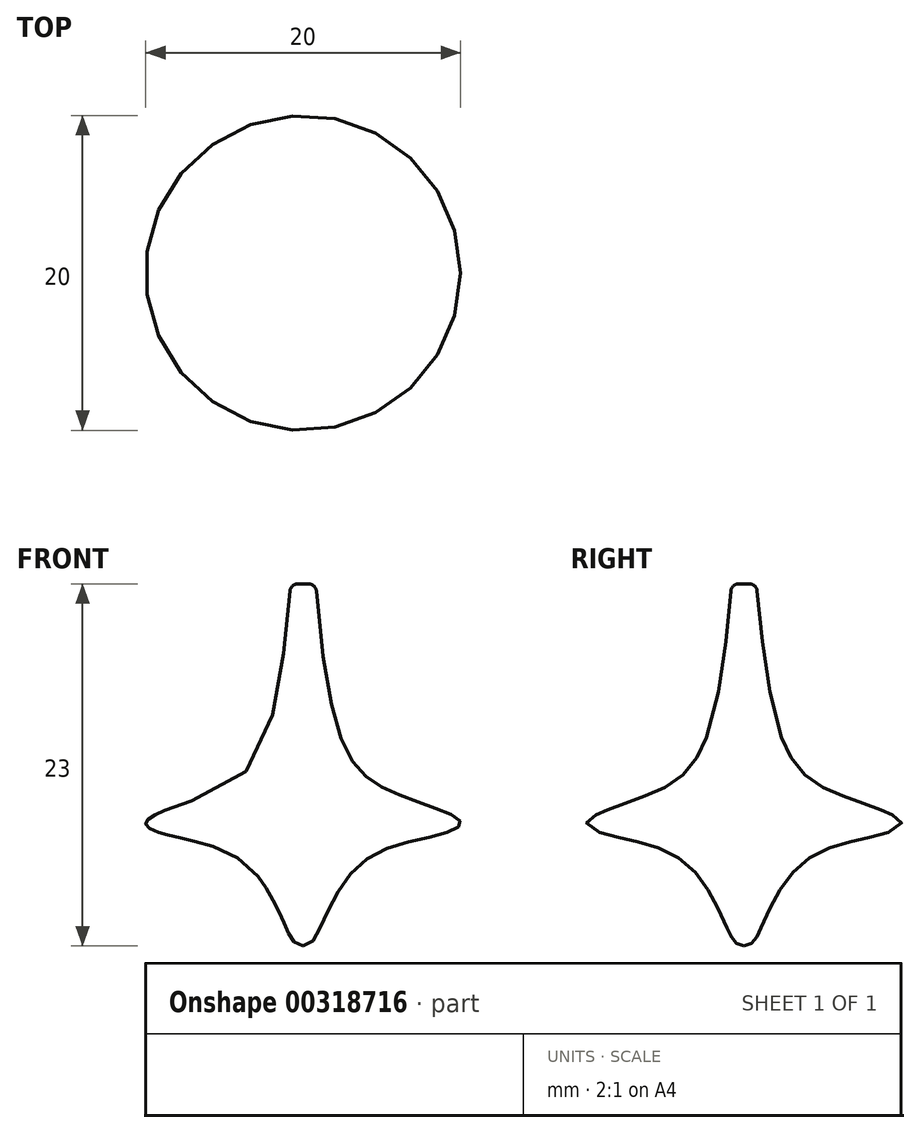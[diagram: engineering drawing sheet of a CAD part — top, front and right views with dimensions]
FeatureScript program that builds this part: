
annotation { "Feature Type Name" : "Feature", "Feature Type Description" : "" }
export const myFeature = defineFeature(function(context is Context, id is Id, definition is map)
    precondition{}
    {
        {
            var Q0;
            Q0=qCreatedBy(makeId("Front.planeOp"),FACE);
            var sketch = newSketch(context, id + "F0", { "sketchPlane" : qUnion([Q0])});
            skLineSegment(sketch, "E0", {"start": v(0, 0) * mm, "end": v(0, 23) * mm});
            skLineSegment(sketch, "E1", {"start": v(0, 23) * mm, "end": v(0.8, 23) * mm});
            skFitSpline(sketch, "E2", {"points": [v(0.8, 23) * mm, v(5, 10.1) * mm, v(8.8, 8.6) * mm, v(10, 7.8) * mm, v(8.8, 7.1) * mm, v(4, 5.5) * mm, v(1.2, 1.4) * mm, v(0, 0) * mm], "startDerivative": vector(9.17, -112.58) * mm, "endDerivative": vector(-18.45, 0) * mm});
            skLineSegment(sketch, "E3", {"start": v(10, 7.8) * mm, "end": v(0, 7.8) * mm, "construction": true});
            skSolve(sketch);
        }
        {
            var Q0;
            Q0=makeQuery(id+"F0.imprint","IMPRINT",FACE,{"disambiguationData":[TD([[makeQuery(id+"F0.imprint","IMPRINT",EDGE,{"derivedFrom":sQuery(id+"F0.wireOp",EDGE,"E0")}),-1.0]])]});
            var Q1;
            Q1=sQuery(id+"F0.wireOp",EDGE,"E0");
            revolve(context, id + "F1", {"entities" : qUnion([Q0]), "axis" : qUnion([Q1]), "revolveType" : RevolveType.FULL});
        }
        {
            var Q0;
            Q0=makeQuery(id+"F1.opRevolve","SWEPT_EDGE",EDGE,{"disambiguationData":[OSD([sQuery(id+"F0.wireOp",EDGE,"E1"),sQuery(id+"F0.wireOp",EDGE,"E2")])]});
            fillet(context, id + "F2", {"entities" : qUnion([Q0]), "radius" : 0.5 * mm, "tangentPropagation" : true, "allowEdgeOverflow" : false});
        }
    });
